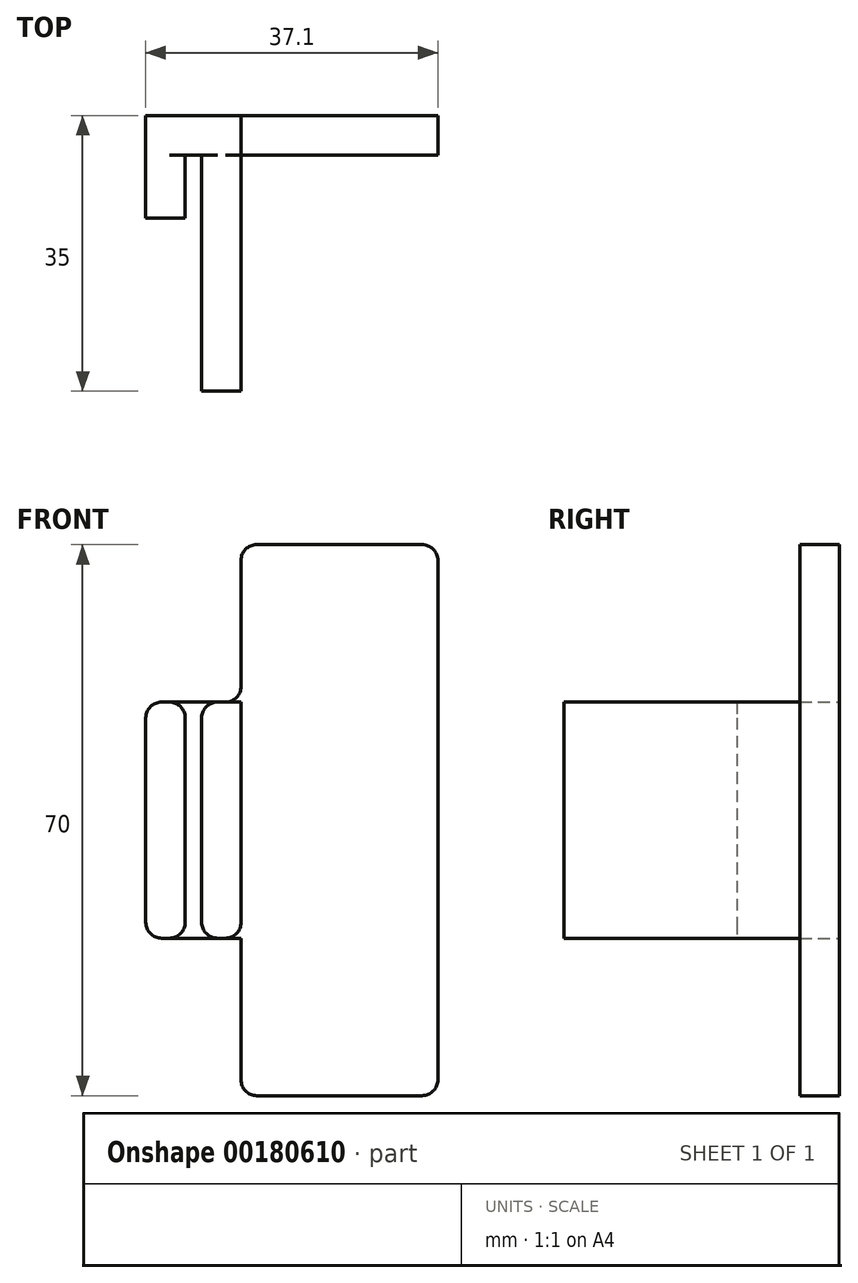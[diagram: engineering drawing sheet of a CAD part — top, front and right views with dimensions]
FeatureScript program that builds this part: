
annotation { "Feature Type Name" : "Feature", "Feature Type Description" : "" }
export const myFeature = defineFeature(function(context is Context, id is Id, definition is map)
    precondition{}
    {
        {
            var Q0;
            Q0=qCreatedBy(makeId("Top.planeOp"),FACE);
            var sketch = newSketch(context, id + "F0", { "sketchPlane" : qUnion([Q0])});
            skLineSegment(sketch, "E0", {"start": v(-12.1, -13) * mm, "end": v(-7.1, -13) * mm});
            skLineSegment(sketch, "E1", {"start": v(-7.1, -13) * mm, "end": v(-7.1, -5) * mm});
            skLineSegment(sketch, "E2", {"start": v(-7.1, -5) * mm, "end": v(-5, -5) * mm});
            skLineSegment(sketch, "E3", {"start": v(-5, -5) * mm, "end": v(-5, -35) * mm});
            skLineSegment(sketch, "E4", {"start": v(-5, -35) * mm, "end": v(0, -35) * mm});
            skLineSegment(sketch, "E5", {"start": v(0, -35) * mm, "end": v(0, 0) * mm});
            skLineSegment(sketch, "E6", {"start": v(25, 0) * mm, "end": v(-12.1, 0) * mm});
            skLineSegment(sketch, "E7", {"start": v(-12.1, 0) * mm, "end": v(-12.1, -13) * mm});
            skPoint(sketch, "E8.visualSharp", {"position": v(0, 0) * mm});
            skPoint(sketch, "E9.visualSharp", {"position": v(0, -35) * mm});
            skPoint(sketch, "E10.visualSharp", {"position": v(-5, -35) * mm});
            skPoint(sketch, "E11.visualSharp", {"position": v(-7.1, -13) * mm});
            skPoint(sketch, "E12.visualSharp", {"position": v(-12.1, -13) * mm});
            skLineSegment(sketch, "E13", {"start": v(0, -5) * mm, "end": v(25, -5) * mm});
            skLineSegment(sketch, "E14", {"start": v(25, -5) * mm, "end": v(25, 0) * mm});
            skPoint(sketch, "E15.visualSharp", {"position": v(0, -5) * mm});
            skPoint(sketch, "E16.visualSharp", {"position": v(25, -5) * mm});
            skPoint(sketch, "E17.visualSharp", {"position": v(25, 0) * mm});
            skPoint(sketch, "E18.visualSharp", {"position": v(-12.1, 0) * mm});
            skSolve(sketch);
        }
        {
            var Q0;
            Q0=makeQuery(id+"F0.imprint","IMPRINT",FACE,{"disambiguationData":[TD([[makeQuery(id+"F0.imprint","IMPRINT",EDGE,{"derivedFrom":sQuery(id+"F0.wireOp",EDGE,"E0")}),1.0]])]});
            extrude(context, id + "F1", {"entities" : qUnion([Q0]), "endBound" : BoundingType.SYMMETRIC, "depth" : 30 * mm});
        }
        {
            var Q0;
            {var subQ0=sQuery(id+"F0.wireOp",EDGE,"E13");Q0=makeQuery(id+"F0.imprint","IMPRINT",FACE,{"disambiguationData":[TD([[makeQuery(id+"F0.imprint","IMPRINT",EDGE,{"derivedFrom":subQ0}),1.0]])]});}
            extrude(context, id + "F2", {"entities" : qUnion([Q0]), "operationType" : NewBodyOperationType.ADD, "endBound" : BoundingType.SYMMETRIC, "depth" : 70 * mm});
        }
        {
            var Q0;
            {var subQ0=sQuery(id+"F0.wireOp",EDGE,"E5");Q0=makeQuery(id+"F2.boolean.opBoolean","SPLIT",EDGE,{"disambiguationData":[topologyDisambiguationEdgeConnected([makeQuery(id+"F2.opExtrude","SWEPT_FACE",FACE,{"disambiguationData":[OSD([subQ0])]})])],"derivedFrom":makeQuery(id+"F1.opExtrude","CAP_EDGE",EDGE,{"disambiguationData":[OSD([subQ0])],"isStart":false})});}
            var Q1;
            {var subQ0=sQuery(id+"F0.wireOp",EDGE,"E5");Q1=makeQuery(id+"F2.boolean.opBoolean","SPLIT",EDGE,{"disambiguationData":[topologyDisambiguationEdgeConnected([makeQuery(id+"F2.opExtrude","SWEPT_FACE",FACE,{"disambiguationData":[OSD([subQ0])]})])],"derivedFrom":makeQuery(id+"F1.opExtrude","CAP_EDGE",EDGE,{"disambiguationData":[OSD([subQ0])],"isStart":true})});}
            var Q2;
            Q2=makeQuery(id+"F2.opExtrude","CAP_EDGE",EDGE,{"disambiguationData":[OSD([sQuery(id+"F0.wireOp",EDGE,"E5")])],"isStart":true});
            var Q3;
            Q3=makeQuery(id+"F2.opExtrude","CAP_EDGE",EDGE,{"disambiguationData":[OSD([sQuery(id+"F0.wireOp",EDGE,"E5")])],"isStart":false});
            var Q4;
            Q4=makeQuery(id+"F2.opExtrude","CAP_EDGE",EDGE,{"disambiguationData":[OSD([sQuery(id+"F0.wireOp",EDGE,"E14")])],"isStart":false});
            var Q5;
            Q5=makeQuery(id+"F2.opExtrude","CAP_EDGE",EDGE,{"disambiguationData":[OSD([sQuery(id+"F0.wireOp",EDGE,"E14")])],"isStart":true});
            var Q6;
            Q6=makeQuery(id+"F1.opExtrude","CAP_EDGE",EDGE,{"disambiguationData":[OSD([sQuery(id+"F0.wireOp",EDGE,"E7")])],"isStart":false});
            var Q7;
            Q7=makeQuery(id+"F1.opExtrude","CAP_EDGE",EDGE,{"disambiguationData":[OSD([sQuery(id+"F0.wireOp",EDGE,"E3")])],"isStart":false});
            var Q8;
            Q8=makeQuery(id+"F1.opExtrude","CAP_EDGE",EDGE,{"disambiguationData":[OSD([sQuery(id+"F0.wireOp",EDGE,"E1")])],"isStart":false});
            var Q9;
            Q9=makeQuery(id+"F1.opExtrude","CAP_EDGE",EDGE,{"disambiguationData":[OSD([sQuery(id+"F0.wireOp",EDGE,"E3")])],"isStart":true});
            var Q10;
            Q10=makeQuery(id+"F1.opExtrude","CAP_EDGE",EDGE,{"disambiguationData":[OSD([sQuery(id+"F0.wireOp",EDGE,"E7")])],"isStart":true});
            var Q11;
            Q11=makeQuery(id+"F1.opExtrude","CAP_EDGE",EDGE,{"disambiguationData":[OSD([sQuery(id+"F0.wireOp",EDGE,"E1")])],"isStart":true});
            fillet(context, id + "F3", {"entities" : qUnion([Q0, Q1, Q2, Q3, Q4, Q5, Q6, Q7, Q8, Q9, Q10, Q11]), "radius" : 2 * mm, "tangentPropagation" : true, "allowEdgeOverflow" : false});
        }
    });
